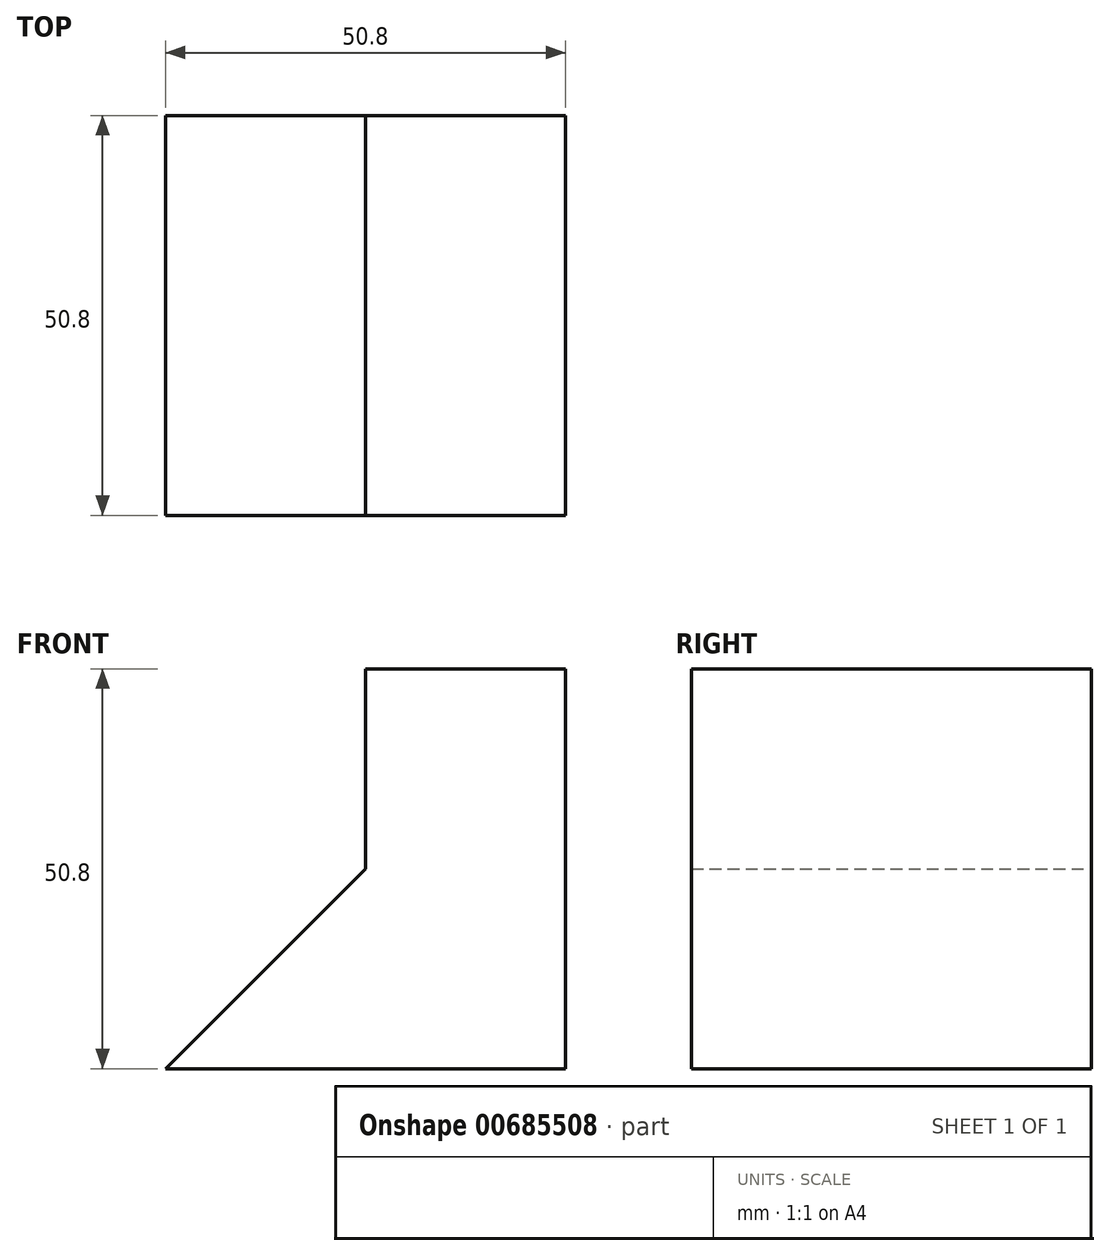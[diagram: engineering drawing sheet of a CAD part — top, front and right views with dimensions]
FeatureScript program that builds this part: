
annotation { "Feature Type Name" : "Feature", "Feature Type Description" : "" }
export const myFeature = defineFeature(function(context is Context, id is Id, definition is map)
    precondition{}
    {
        {
            var Q0;
            Q0=qCreatedBy(makeId("Front.planeOp"),FACE);
            var sketch = newSketch(context, id + "F0", { "sketchPlane" : qUnion([Q0])});
            skLineSegment(sketch, "E0.bottom", {"start": v(0, 0) * mm, "end": v(50.8, 0) * mm});
            skLineSegment(sketch, "E0.top", {"start": v(25.4, 50.8) * mm, "end": v(50.8, 50.8) * mm});
            skLineSegment(sketch, "E0.right", {"start": v(50.8, 0) * mm, "end": v(50.8, 50.8) * mm});
            skLineSegment(sketch, "E1.right", {"start": v(25.4, 50.8) * mm, "end": v(25.4, 25.4) * mm});
            skLineSegment(sketch, "E2", {"start": v(25.4, 25.4) * mm, "end": v(0, 0) * mm});
            skSolve(sketch);
        }
        {
            var Q0;
            Q0=makeQuery(id+"F0.imprint","IMPRINT",FACE,{"disambiguationData":[TD([[makeQuery(id+"F0.imprint","IMPRINT",EDGE,{"derivedFrom":sQuery(id+"F0.wireOp",EDGE,"E0.bottom")}),1.0]])]});
            extrude(context, id + "F1", {"entities" : qUnion([Q0]), "depth" : 50.8 * mm, "offsetDistance" : 25.4 * mm});
        }
    });
